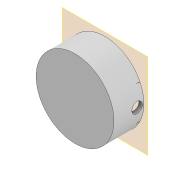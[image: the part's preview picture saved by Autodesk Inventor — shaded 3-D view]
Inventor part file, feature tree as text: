
AUTODESK INVENTOR PART (.ipt)
format: ipt  version: 2022 (Build 260153000, 153)  size: 997,888 bytes
history: native  units: mm
features: extrude x7, sketch x7, other x6, reference x4, projected_geometry x4, plane x2
ambient origin geometry x8: Origin, YZ Plane, XZ Plane, XY Plane, X Axis, Y Axis, Z Axis, Center Point
bodies: Volumenkörper1 (feature_tree)
feature tree (30):
  plane  "Arbeitsebene1"
  extrude  "Extrusion1"  Depth=18.0mm TaperAngle=0.0deg
  extrude  "Extrusion2"  Depth=18.0mm TaperAngle=0.0deg
  sketch  "Skizze3"  dims[d7=10.0mm d8=0.0mm d9=0.5mm]
  plane  "Arbeitsebene2"
  extrude  "Extrusion3"  Depth=10.0mm
  extrude  "Extrusion4"  TaperAngle=180.0deg  [1 undecoded]
  extrude  "Extrusion5"  Depth=7.0mm
  extrude  "Extrusion6"  [1 undecoded]
  extrude  "Extrusion7"  [1 undecoded]
  sketch  "Skizze1"  dims[d0=2.0mm d1=18.0mm d2=0.0mm]
  reference  "Referenz1"
  sketch  "Skizze2"  dims[d3=2.0mm d4=0.0mm d5=18.0mm d6=0.0mm]
  reference  "Referenz2"
  sketch  "Skizze4"  dims[d10=4.3mm d11=0.0mm d18=180.0deg]
  reference  "Referenz3"
  projected_geometry  "Projizierte Kontur1"
  projected_geometry  "Projizierte Kontur2"
  projected_geometry  "Projizierte Kontur3"
  projected_geometry  "Projizierte Kontur4"
  sketch  "Skizze5"  dims[d19=23.0mm d20=0.0mm d21=7.0mm]
  reference  "Referenz4"
  sketch  "Skizze7"  dims[d22=23.0mm d23=0.0mm]
  sketch  "Skizze8"
  other  "Planktoscope_Mini_v0.iam"
  other  "Planktoscope_Mini_Peristalticpump:1"
  other  "Pump_Base_Motor:1"
  other  "Planktoscope_Mini_Electronicbase.iam"
  other  "00_ULN2003 Stepper Driver:1"
  other  "00_Wemos-Mini-D1-ESP32:1"
note: 3 required parameter values undecoded (feature->parameter linkage not recoverable at this tier; creation-order binding heuristic only, values carry confidence <= 0.55)
